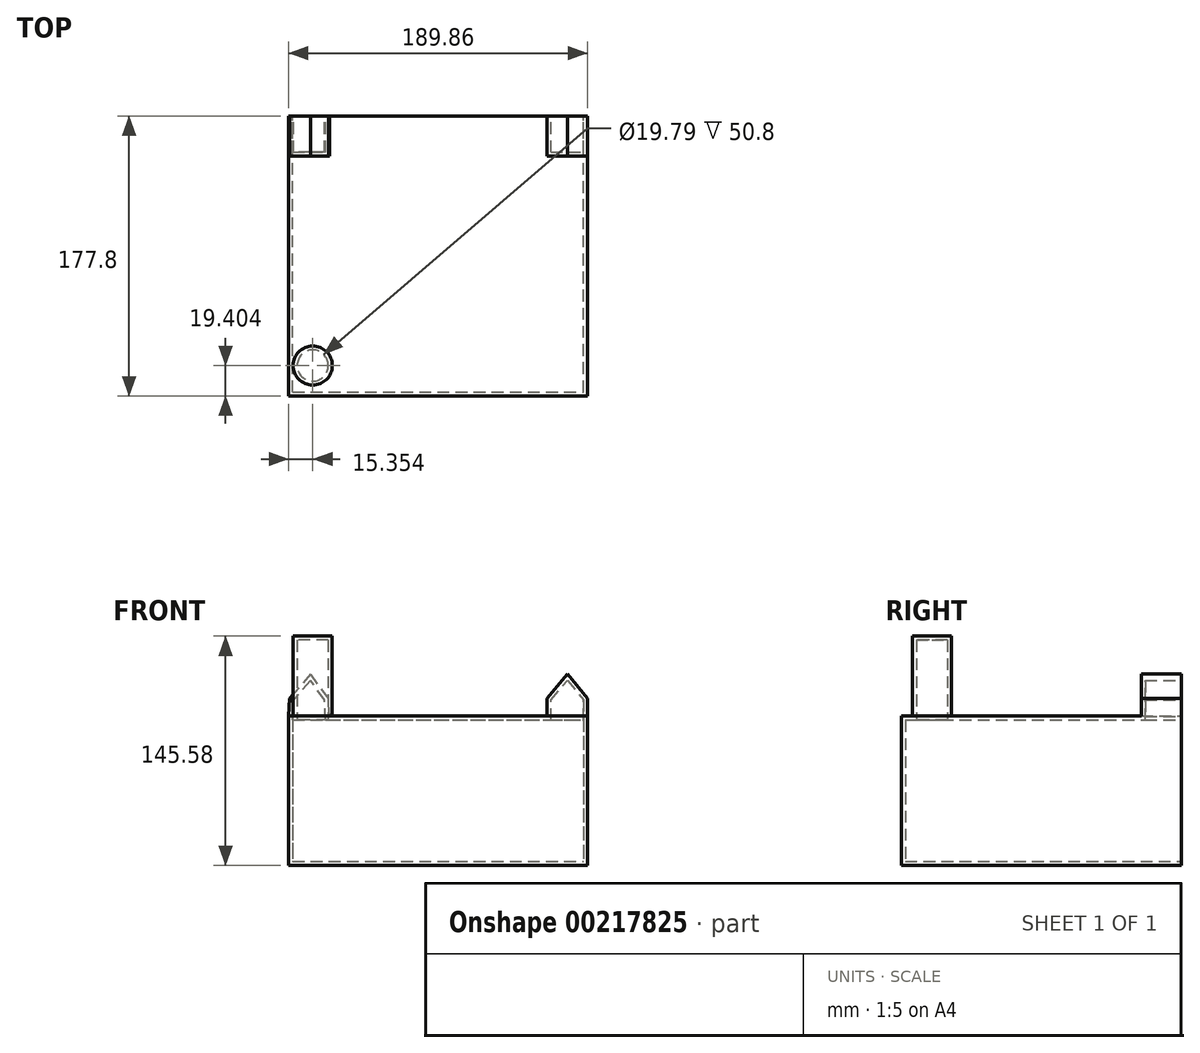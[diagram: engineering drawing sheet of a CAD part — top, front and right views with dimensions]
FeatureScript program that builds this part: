
annotation { "Feature Type Name" : "Feature", "Feature Type Description" : "" }
export const myFeature = defineFeature(function(context is Context, id is Id, definition is map)
    precondition{}
    {
        {
            var Q0;
            Q0=qCreatedBy(makeId("Front.planeOp"),FACE);
            var sketch = newSketch(context, id + "F0", { "sketchPlane" : qUnion([Q0])});
            skLineSegment(sketch, "E0.bottom", {"start": v(-92.3, 45.14) * mm, "end": v(97.57, 45.14) * mm});
            skLineSegment(sketch, "E0.top", {"start": v(-92.3, -49.64) * mm, "end": v(97.57, -49.64) * mm});
            skLineSegment(sketch, "E0.left", {"start": v(-92.3, 45.14) * mm, "end": v(-92.3, -49.64) * mm});
            skLineSegment(sketch, "E0.right", {"start": v(97.57, 45.14) * mm, "end": v(97.57, -49.64) * mm});
            skLineSegment(sketch, "E1", {"start": v(-66.37, 45.14) * mm, "end": v(-66.96, 56.39) * mm});
            skLineSegment(sketch, "E2", {"start": v(-66.96, 56.39) * mm, "end": v(-78.2, 71.85) * mm});
            skLineSegment(sketch, "E3", {"start": v(-78.2, 71.85) * mm, "end": v(-91.52, 56.39) * mm});
            skLineSegment(sketch, "E4", {"start": v(-91.52, 56.39) * mm, "end": v(-92.3, 45.14) * mm});
            skLineSegment(sketch, "E5", {"start": v(97.57, 45.14) * mm, "end": v(97.57, 56.39) * mm});
            skLineSegment(sketch, "E6", {"start": v(71.71, 45.14) * mm, "end": v(71.71, 56.39) * mm});
            skLineSegment(sketch, "E7", {"start": v(71.71, 58.64) * mm, "end": v(81.28, 69.89) * mm});
            skLineSegment(sketch, "E8", {"start": v(71.71, 56.39) * mm, "end": v(84.86, 71.85) * mm});
            skLineSegment(sketch, "E9", {"start": v(84.86, 71.85) * mm, "end": v(97.57, 56.39) * mm});
            skSolve(sketch);
        }
        {
            var Q0;
            Q0=makeQuery(id+"F0.imprint","IMPRINT",FACE,{"disambiguationData":[TD([[makeQuery(id+"F0.imprint","IMPRINT",EDGE,{"derivedFrom":sQuery(id+"F0.wireOp",EDGE,"E0.top")}),1.0]])]});
            extrude(context, id + "F1", {"entities" : qUnion([Q0]), "depth" : 177.8 * mm});
        }
        {
            var Q0;
            {var subQ0=sQuery(id+"F0.wireOp",EDGE,"E1");Q0=makeQuery(id+"F0.imprint","IMPRINT",FACE,{"disambiguationData":[TD([[makeQuery(id+"F0.imprint","IMPRINT",EDGE,{"derivedFrom":subQ0}),1.0]])]});}
            var Q1;
            {var subQ1=sQuery(id+"F0.wireOp",EDGE,"E5");Q1=makeQuery(id+"F0.imprint","IMPRINT",FACE,{"disambiguationData":[TD([[makeQuery(id+"F0.imprint","IMPRINT",EDGE,{"derivedFrom":subQ1}),1.0]])]});}
            extrude(context, id + "F2", {"entities" : qUnion([Q0, Q1]), "operationType" : NewBodyOperationType.ADD, "depth" : 25.4 * mm});
        }
        {
            var Q0;
            Q0=makeQuery(id+"F1.opExtrude","SWEPT_FACE",FACE,{"disambiguationData":[OSD([sQuery(id+"F0.wireOp",EDGE,"E0.bottom")])]});
            var sketch = newSketch(context, id + "F3", { "sketchPlane" : qUnion([Q0])});
            skCircle(sketch, "E10", {"center": v(-76.94, -158.4) * mm, "radius": 13.15 * mm});
            skCircle(sketch, "E11", {"center": v(-76.94, -158.4) * mm, "radius": 12.44 * mm});
            skSolve(sketch);
        }
        {
            var Q0;
            Q0=makeQuery(id+"F3.imprint","IMPRINT",FACE,{"disambiguationData":[TD([[makeQuery(id+"F3.imprint","IMPRINT",EDGE,{"derivedFrom":sQuery(id+"F3.wireOp",EDGE,"E11")}),1.0]])]});
            extrude(context, id + "F4", {"entities" : qUnion([Q0]), "operationType" : NewBodyOperationType.ADD, "depth" : 50.8 * mm});
        }
        {
            var Q0;
            {var subQ0=sQuery(id+"F0.wireOp",EDGE,"E0.bottom");Q0=makeQuery(id+"F2.boolean.opBoolean","MERGE",FACE,{"derivedFrom":[makeQuery(id+"F1.opExtrude","CAP_FACE",FACE,{"disambiguationData":[OSD([subQ0,sQuery(id+"F0.wireOp",EDGE,"E0.top"),sQuery(id+"F0.wireOp",EDGE,"E0.left"),sQuery(id+"F0.wireOp",EDGE,"E0.right")])],"isStart":true}),makeQuery(id+"F2.opExtrude","CAP_FACE",FACE,{"disambiguationData":[OSD([subQ0,sQuery(id+"F0.wireOp",EDGE,"E1"),sQuery(id+"F0.wireOp",EDGE,"E2"),sQuery(id+"F0.wireOp",EDGE,"E3"),sQuery(id+"F0.wireOp",EDGE,"E4")])],"isStart":true}),makeQuery(id+"F2.opExtrude","CAP_FACE",FACE,{"disambiguationData":[OSD([subQ0,sQuery(id+"F0.wireOp",EDGE,"E5"),sQuery(id+"F0.wireOp",EDGE,"E6"),sQuery(id+"F0.wireOp",EDGE,"E8"),sQuery(id+"F0.wireOp",EDGE,"E9")])],"isStart":true})]});}
            shell(context, id + "F5", {"entities" : qUnion([Q0]), "thickness" : 2.54 * mm});
        }
        {
            var Q0;
            Q0=qCreatedBy(makeId("Top.planeOp"),FACE);
            var sketch = newSketch(context, id + "F6", { "sketchPlane" : qUnion([Q0])});
            skCircle(sketch, "E12", {"center": v(82.28, -160.42) * mm, "radius": 13.13 * mm});
            skSolve(sketch);
        }
        {
            var Q0;
            Q0=sQuery(id+"F6.wireOp",EDGE,"E12");
            extrude(context, id + "F7", {"bodyType" : ToolBodyType.SURFACE, "surfaceEntities" : qUnion([Q0]), "depth" : 97.28 * mm});
        }
    });
